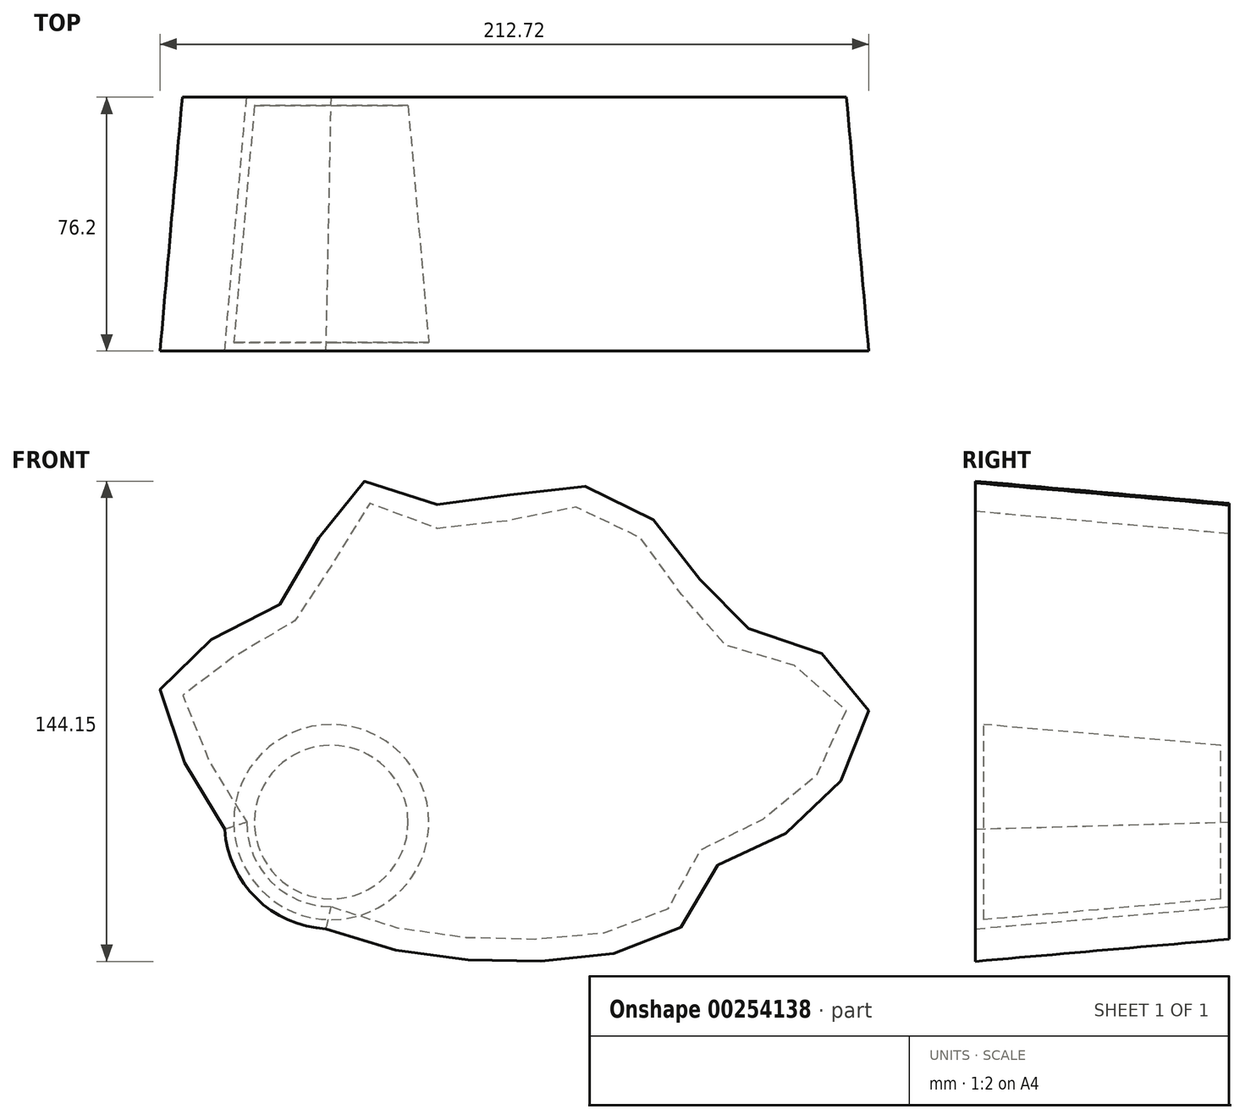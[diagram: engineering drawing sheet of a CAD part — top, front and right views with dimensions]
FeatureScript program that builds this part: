
annotation { "Feature Type Name" : "Feature", "Feature Type Description" : "" }
export const myFeature = defineFeature(function(context is Context, id is Id, definition is map)
    precondition{}
    {
        {
            var Q0;
            Q0=qCreatedBy(makeId("Front.planeOp"),FACE);
            var sketch = newSketch(context, id + "F0", { "sketchPlane" : qUnion([Q0])});
            skPoint(sketch, "E0.middle", {"position": v(0, 0) * mm});
            skPoint(sketch, "E1.visualSharp", {"position": v(-76.2, 50.8) * mm});
            skPoint(sketch, "E2.visualSharp", {"position": v(76.2, 50.8) * mm});
            skPoint(sketch, "E3.visualSharp", {"position": v(-76.2, -50.8) * mm});
            skArc(sketch, "E3.filletArc", {"start": v(-76.2, -25.4) * mm, "mid": v(-68.76, -43.36) * mm, "end": v(-50.8, -50.8) * mm});
            skPoint(sketch, "E4.visualSharp", {"position": v(76.2, -50.8) * mm});
            skFitSpline(sketch, "E5", {"points": [v(-50.8, 50.8) * mm, v(-76.2, 25.4) * mm, v(-95.06, 17.41) * mm, v(-76.2, -25.4) * mm, v(-50.8, -50.8) * mm, v(9.9, -60.48) * mm, v(50.8, -50.8) * mm, v(54.37, -39.3) * mm, v(76.2, -25.4) * mm, v(84.73, -21.41) * mm, v(103.8, 8) * mm, v(76.2, 25.4) * mm, v(58.14, 32.95) * mm, v(50.8, 50.8) * mm, v(16.02, 69.66) * mm, v(-11.99, 61.18) * mm, v(-40.7, 70.13) * mm, v(-50.8, 50.8) * mm]});
            skSolve(sketch);
        }
        {
            var Q0;
            Q0 = qSketchRegion(id + "F0", true);
            extrude(context, id + "F1", {"entities" : qUnion([Q0]), "depth" : 76.2 * mm, "hasDraft" : true, "draftAngle" : 5 * degree});
        }
        {
            var Q0;
            Q0=makeQuery(id+"F1.opExtrude","SWEPT_FACE",FACE,{"disambiguationData":[OSD([sQuery(id+"F0.wireOp",EDGE,"E5")])]});
            shell(context, id + "F2", {"entities" : qUnion([Q0]), "thickness" : 2.54 * mm});
        }
    });
